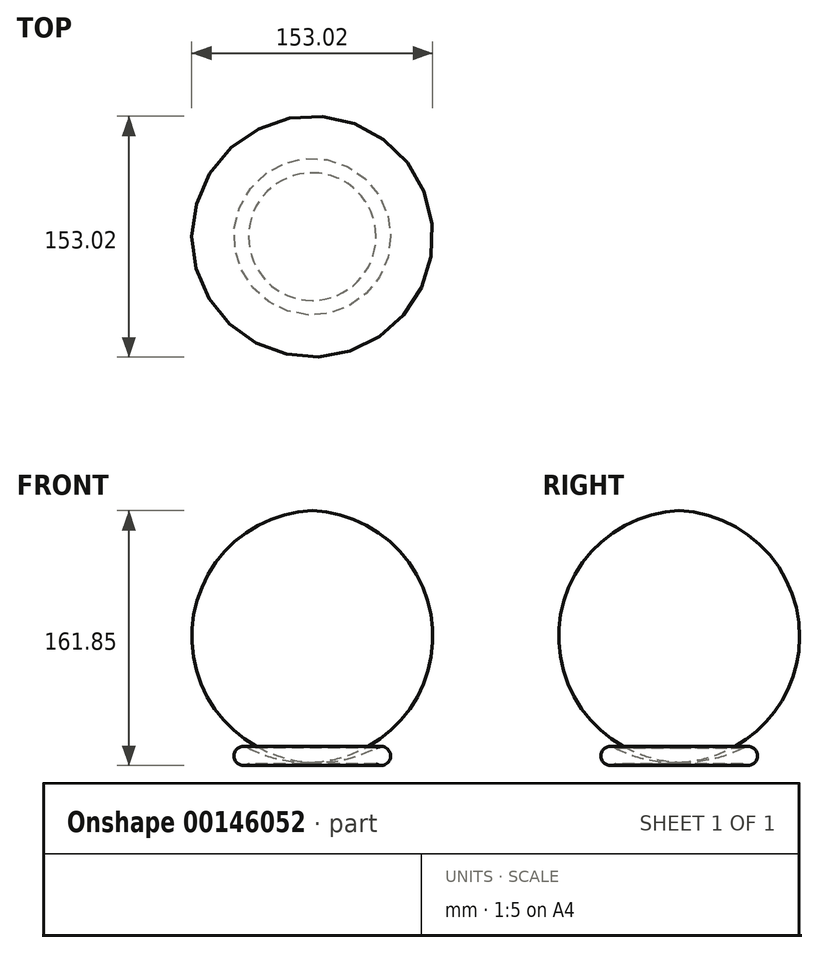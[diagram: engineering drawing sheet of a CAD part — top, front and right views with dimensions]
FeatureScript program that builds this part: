
annotation { "Feature Type Name" : "Feature", "Feature Type Description" : "" }
export const myFeature = defineFeature(function(context is Context, id is Id, definition is map)
    precondition{}
    {
        {
            var Q0;
            Q0=qCreatedBy(makeId("Front.planeOp"),FACE);
            var sketch = newSketch(context, id + "F0", { "sketchPlane" : qUnion([Q0])});
            skLineSegment(sketch, "E0.bottom", {"start": v(0, 0) * mm, "end": v(-40.5, 0) * mm});
            skLineSegment(sketch, "E0.right", {"start": v(-40.5, 0) * mm, "end": v(-40.5, 10) * mm, "construction": true});
            skArc(sketch, "E1", {"start": v(-40.5, 10) * mm, "mid": v(-49.82, 5) * mm, "end": v(-40.5, 0) * mm});
            skLineSegment(sketch, "E2", {"start": v(-40.5, 0) * mm, "end": v(-47.13, 0) * mm, "construction": true});
            skLineSegment(sketch, "E3", {"start": v(0, 0) * mm, "end": v(0, 1) * mm});
            skArc(sketch, "E4", {"start": v(-40.5, 10) * mm, "mid": v(-20.84, 2.83) * mm, "end": v(0, 1) * mm});
            skLineSegment(sketch, "E5", {"start": v(0, 20.8) * mm, "end": v(0, -15.43) * mm, "construction": true});
            skSolve(sketch);
        }
        {
            var Q0;
            Q0=makeQuery(id+"F0.imprint","IMPRINT",FACE,{"disambiguationData":[TD([[makeQuery(id+"F0.imprint","IMPRINT",EDGE,{"derivedFrom":sQuery(id+"F0.wireOp",EDGE,"E0.bottom")}),-1.0]])]});
            var Q1;
            Q1=sQuery(id+"F0.wireOp",EDGE,"E5");
            revolve(context, id + "F1", {"entities" : qUnion([Q0]), "axis" : qUnion([Q1]), "revolveType" : RevolveType.FULL});
        }
    });
